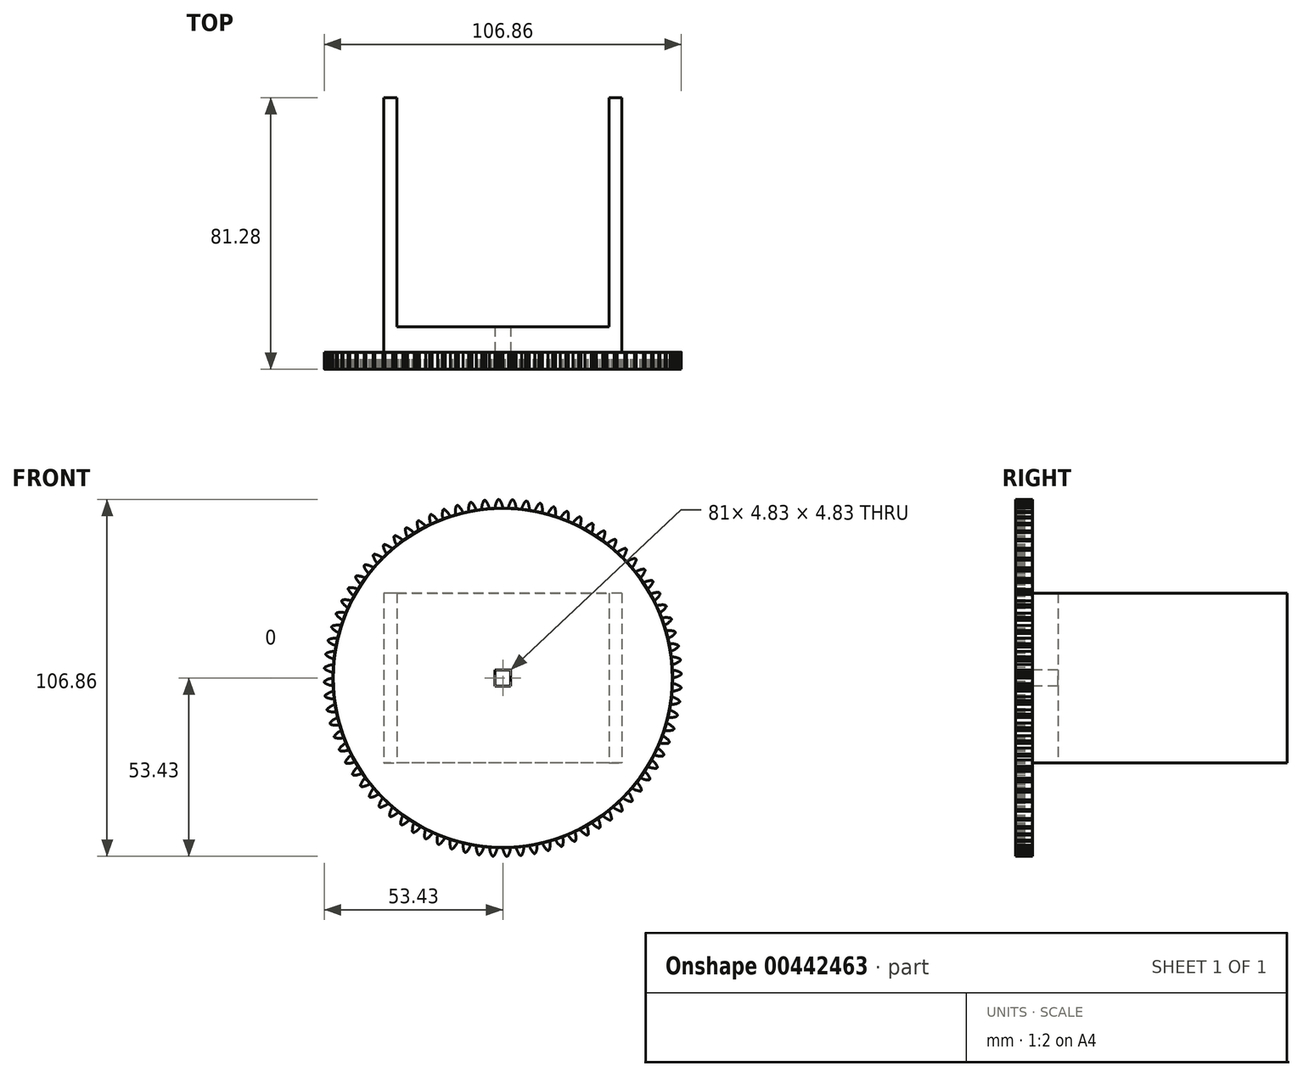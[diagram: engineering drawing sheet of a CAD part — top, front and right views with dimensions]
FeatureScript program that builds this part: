
annotation { "Feature Type Name" : "Feature", "Feature Type Description" : "" }
export const myFeature = defineFeature(function(context is Context, id is Id, definition is map)
    precondition{}
    {
        {
            var Q0;
            Q0=qCreatedBy(makeId("Front.planeOp"),FACE);
            var sketch = newSketch(context, id + "F0", { "sketchPlane" : qUnion([Q0])});
            skCircle(sketch, "E0", {"center": v(0, 0) * mm, "radius": 50.8 * mm});
            skCircle(sketch, "E1", {"center": v(0, 0) * mm, "radius": 51.94 * mm, "construction": true});
            skCircle(sketch, "E2", {"center": v(0, 0) * mm, "radius": 53.21 * mm, "construction": true});
            skLineSegment(sketch, "E3", {"start": v(0, 0) * mm, "end": v(0, 131.57) * mm, "construction": true});
            skLineSegment(sketch, "E4", {"start": v(0, 0) * mm, "end": v(-1.17, 50.79) * mm, "construction": true});
            skLineSegment(sketch, "E5", {"start": v(-1.17, 50.79) * mm, "end": v(-1.51, 65.77) * mm, "construction": true});
            skLineSegment(sketch, "E6", {"start": v(0, 51.94) * mm, "end": v(-78.8, 51.94) * mm, "construction": true});
            skLineSegment(sketch, "E7", {"start": v(0, 51.94) * mm, "end": v(-14.03, 49.48) * mm, "construction": true});
            skArc(sketch, "E8", {"start": v(0, 50.8) * mm, "mid": v(-0.3, 52.05) * mm, "end": v(-0.87, 53.2) * mm});
            skArc(sketch, "E9.MirrorCS", {"start": v(-2.33, 50.75) * mm, "mid": v(-2.1, 52) * mm, "end": v(-1.6, 53.18) * mm});
            skArc(sketch, "E10", {"start": v(-0.87, 53.2) * mm, "mid": v(-1.24, 53.43) * mm, "end": v(-1.6, 53.18) * mm});
            skSolve(sketch);
        }
        {
            var Q0;
            Q0 = qSketchRegion(id + "F0", true);
            extrude(context, id + "F1", {"entities" : qUnion([Q0]), "depth" : 5.08 * mm, "offsetDistance" : 25.4 * mm});
        }
        {
            var Q0;
            Q0=makeQuery(id+"F1.opExtrude","SWEPT_BODY",BODY,{"disambiguationData":[OSD([sQuery(id+"F0.wireOp",EDGE,"E0"),sQuery(id+"F0.wireOp",EDGE,"E8"),sQuery(id+"F0.wireOp",EDGE,"E9.MirrorCS"),sQuery(id+"F0.wireOp",EDGE,"E10")])]});
            var Q1;
            Q1=makeQuery(id+"F1.opExtrude","SWEPT_FACE",FACE,{"disambiguationData":[OSD([sQuery(id+"F0.wireOp",EDGE,"E0")])]});
            circularPattern(context, id + "F2", {"entities" : qUnion([Q0]), "axis" : qUnion([Q1]), "angle" : 360 * degree, "instanceCount" : 80, "equalSpace" : true});
        }
        {
            var Q0;
            Q0=makeQuery(id+"F2.opPattern","COPY",FACE,{"derivedFrom":makeQuery(id+"F1.opExtrude","CAP_FACE",FACE,{"disambiguationData":[OSD([sQuery(id+"F0.wireOp",EDGE,"E0"),sQuery(id+"F0.wireOp",EDGE,"E8"),sQuery(id+"F0.wireOp",EDGE,"E9.MirrorCS"),sQuery(id+"F0.wireOp",EDGE,"E10")])],"isStart":false}),"instanceName":"40"});
            var sketch = newSketch(context, id + "F3", { "sketchPlane" : qUnion([Q0])});
            skLineSegment(sketch, "E11.bottom", {"start": v(2.41, -2.41) * mm, "end": v(-2.41, -2.41) * mm});
            skLineSegment(sketch, "E11.top", {"start": v(2.41, 2.41) * mm, "end": v(-2.41, 2.41) * mm});
            skLineSegment(sketch, "E11.left", {"start": v(2.41, -2.41) * mm, "end": v(2.41, 2.41) * mm});
            skLineSegment(sketch, "E11.right", {"start": v(-2.41, -2.41) * mm, "end": v(-2.41, 2.41) * mm});
            skPoint(sketch, "E11.middle", {"position": v(0, 0) * mm});
            skSolve(sketch);
        }
        {
            var Q0;
            Q0=qCreatedBy(makeId("Right.planeOp"),FACE);
            var sketch = newSketch(context, id + "F4", { "sketchPlane" : qUnion([Q0])});
            skLineSegment(sketch, "E12.bottom", {"start": v(76.2, 25.4) * mm, "end": v(0, 25.4) * mm});
            skLineSegment(sketch, "E12.top", {"start": v(76.2, -25.4) * mm, "end": v(0, -25.4) * mm});
            skLineSegment(sketch, "E12.left", {"start": v(76.2, 25.4) * mm, "end": v(76.2, -25.4) * mm});
            skLineSegment(sketch, "E12.right", {"start": v(0, 25.4) * mm, "end": v(0, -25.4) * mm});
            skSolve(sketch);
        }
        {
            var Q0;
            Q0 = qSketchRegion(id + "F4", true);
            extrude(context, id + "F5", {"entities" : qUnion([Q0]), "depth" : 35.56 * mm, "offsetDistance" : 25.4 * mm, "hasSecondDirection" : true, "secondDirectionOppositeDirection" : true, "secondDirectionDepth" : 35.56 * mm});
        }
        {
            var Q0;
            Q0=qCreatedBy(makeId("Right.planeOp"),FACE);
            var sketch = newSketch(context, id + "F6", { "sketchPlane" : qUnion([Q0])});
            skLineSegment(sketch, "E13.bottom", {"start": v(7.62, 25.4) * mm, "end": v(76.2, 25.4) * mm});
            skLineSegment(sketch, "E13.top", {"start": v(7.62, -25.4) * mm, "end": v(76.2, -25.4) * mm});
            skLineSegment(sketch, "E13.left", {"start": v(7.62, 25.4) * mm, "end": v(7.62, -25.4) * mm});
            skLineSegment(sketch, "E13.right", {"start": v(76.2, 25.4) * mm, "end": v(76.2, -25.4) * mm});
            skSolve(sketch);
        }
        {
            var Q0;
            Q0 = qSketchRegion(id + "F6", true);
            extrude(context, id + "F7", {"entities" : qUnion([Q0]), "operationType" : NewBodyOperationType.REMOVE, "oppositeDirection" : true, "depth" : 31.75 * mm, "offsetDistance" : 25.4 * mm, "hasSecondDirection" : true, "secondDirectionOppositeDirection" : false, "secondDirectionDepth" : 31.75 * mm});
        }
        {
            var Q0;
            Q0 = qSketchRegion(id + "F3", true);
            extrude(context, id + "F8", {"entities" : qUnion([Q0]), "operationType" : NewBodyOperationType.REMOVE, "oppositeDirection" : true, "depth" : 25.4 * mm, "offsetDistance" : 25.4 * mm});
        }
    });
